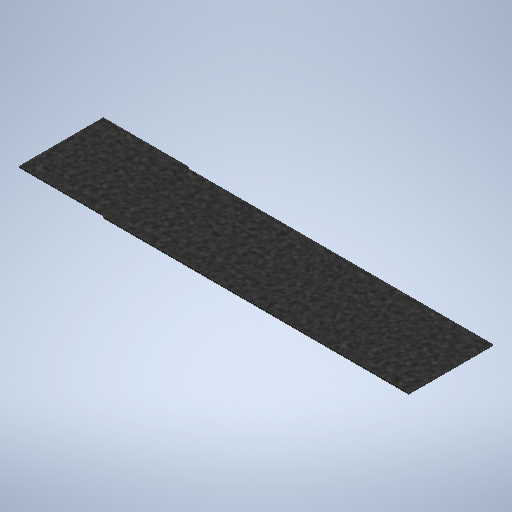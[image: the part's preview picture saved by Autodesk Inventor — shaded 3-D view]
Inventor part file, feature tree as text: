
AUTODESK INVENTOR PART (.ipt)
format: ipt  version: 2025 (Build 290162010, 162A)  size: 283,136 bytes
history: native  units: in
note: dims shown in document units (in); Inventor stores cm internally (conversion verified against a paired STEP export)
features: extrude x1, sketch x1
ambient origin geometry x8: Origin, YZ Plane, XZ Plane, XY Plane, X Axis, Y Axis, Z Axis, Center Point
bodies: Body1 (feature_tree)
feature tree (2):
  extrude  "Extrusion2"  Depth=0.125in
  sketch  "Sketch1"  dims[d0=6.5in d1=0.125in d2=0.125in d3=0.125in d4=0.125in d8=6.5in d9=0.0in d10=23.804in]
